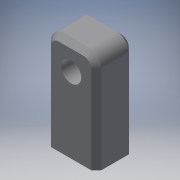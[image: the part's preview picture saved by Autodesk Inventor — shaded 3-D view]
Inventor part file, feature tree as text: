
AUTODESK INVENTOR PART (.ipt)
format: ipt  version: 2017 (Build 210142000, 142)  size: 190,976 bytes
history: native  units: mm
features: extrude x6, sketch x5, chamfer x3, projected_geometry x2, fillet x1
ambient origin geometry x8: Origin, YZ Plane, XZ Plane, XY Plane, X Axis, Y Axis, Z Axis, Center Point
bodies: Solid1 (feature_tree)
feature tree (17):
  sketch  "Sketch1"  dims[d0=15.0mm d1=20.0mm]
  extrude  "Extrusion1"  Depth=20.0mm
  extrude  "Extrusion2"  Depth=15.0mm TaperAngle=0.0deg
  extrude  "Extrusion3"  Depth=10.0mm
  fillet  "Fillet1"  Radius=10.0mm
  extrude  "Extrusion4"  Depth=5.0mm
  chamfer  "Chamfer1"  Distance=25.0mm
  chamfer  "Chamfer2"  Distance=2.0mm Angle=45.0deg
  extrude  "Extrusion5"  Depth=4.0mm TaperAngle=45.0deg
  extrude  "Extrusion6"  TaperAngle=0.0deg  [1 undecoded]
  chamfer  "Chamfer3"  Distance=6.0mm
  sketch  "Sketch2"  dims[d2=6.0mm d3=15.0mm d4=0.0mm]
  sketch  "Sketch3"  dims[d5=25.0mm d6=0.0mm d7=8.0mm d8=10.0mm]
  sketch  "Sketch4"  dims[d9=25.0mm d10=0.0mm d11=5.0mm]
  projected_geometry  "Projected Loop1"
  sketch  "Sketch5"  dims[d12=4.3mm d13=25.0mm d14=0.0mm d15=2.0mm d16=2.0mm d17=45.0deg d18=4.0mm d19=2.0mm d20=45.0deg d21=0.0mm d22=0.0mm d23=6.0mm d24=6.0mm d25=10.0mm d26=0.0mm d27=2.0mm d28=2.0mm d29=45.0deg]
  projected_geometry  "Projected Loop2"
note: 1 required parameter value undecoded (feature->parameter linkage not recoverable at this tier; creation-order binding heuristic only, values carry confidence <= 0.55)
